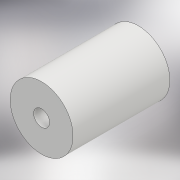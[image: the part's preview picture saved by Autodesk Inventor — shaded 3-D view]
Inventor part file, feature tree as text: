
AUTODESK INVENTOR PART (.ipt)
format: ipt  version: 2018.2 (Build 222227000, 227)  size: 101,888 bytes
history: native  units: mm
features: extrude x1, sketch x1
ambient origin geometry x8: Origin, YZ Plane, XZ Plane, XY Plane, X Axis, Y Axis, Z Axis, Center Point
bodies: Solid1 (feature_tree)
feature tree (2):
  extrude  "Extrusion1"  Depth=20.0mm
  sketch  "Sketch1"  dims[d0=3.3mm d1=13.0mm d2=20.0mm d3=0.0mm]
